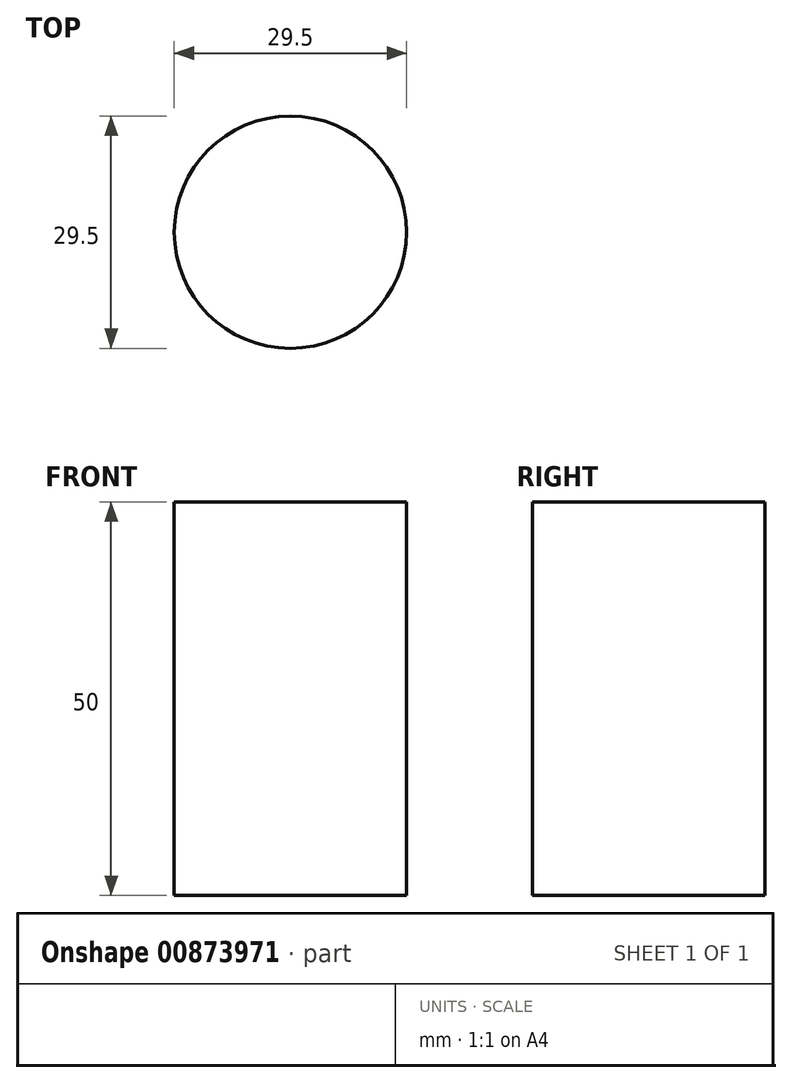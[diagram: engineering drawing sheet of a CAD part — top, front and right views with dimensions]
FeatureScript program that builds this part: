
annotation { "Feature Type Name" : "Feature", "Feature Type Description" : "" }
export const myFeature = defineFeature(function(context is Context, id is Id, definition is map)
    precondition{}
    {
        {
            var Q0;
            Q0=qCreatedBy(makeId("Top.planeOp"),FACE);
            var sketch = newSketch(context, id + "F0", { "sketchPlane" : qUnion([Q0])});
            skCircle(sketch, "E0", {"center": v(0, 0) * mm, "radius": 14.75 * mm});
            skSolve(sketch);
        }
        {
            var Q0;
            Q0 = qSketchRegion(id + "F0", true);
            extrude(context, id + "F1", {"entities" : qUnion([Q0]), "depth" : 50 * mm, "offsetDistance" : 25 * mm});
        }
    });
